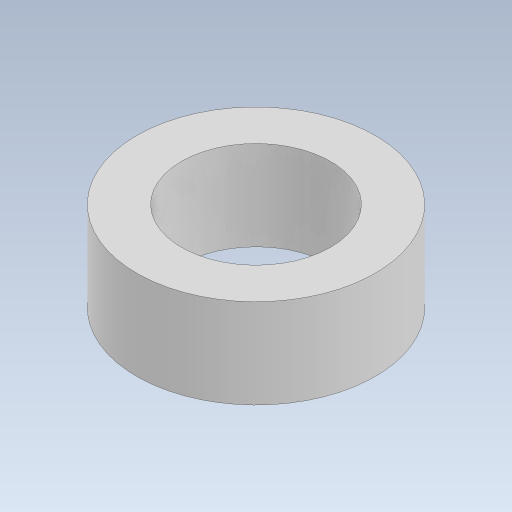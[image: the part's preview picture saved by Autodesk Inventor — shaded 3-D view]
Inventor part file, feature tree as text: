
AUTODESK INVENTOR PART (.ipt)
format: ipt  version: 2023.5 (Build 275446000, 446)  size: 249,856 bytes
history: native  units: mm
features: extrude x1, sketch x1
ambient origin geometry x8: Origin, YZ Plane, XZ Plane, XY Plane, X Axis, Y Axis, Z Axis, Center Point
bodies: Solid1 (feature_tree)
feature tree (2):
  extrude  "Extrusion1"  Depth=3.0mm
  sketch  "Sketch1"  dims[d0=5.0mm d1=8.0mm d2=3.0mm d3=0.0mm]
